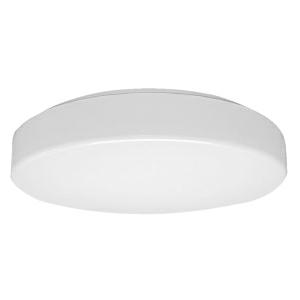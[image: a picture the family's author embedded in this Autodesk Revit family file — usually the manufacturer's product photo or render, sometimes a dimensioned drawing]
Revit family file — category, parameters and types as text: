
# Revit family: oblo_fit_-_oba_1000_840_00813345_71a7
name_source: partatom
category: Lighting Fixtures
units: mm (PartAtom-declared; Revit-internal decimal feet)

## family parameters
Cut with Voids When Loaded = No
Host = Face
Light Source = No
Part Type = Normal
Room Calculation Point = No
Round Connector Dimension = Use Diameter
Shared = No

## types (1)
- OBLO.fit - OBA 1000/840 (1 x LED, 1500 lm, 4000K)
    Apparent Load = 11 VA
    Approval mark = CE
    CIE Flux Codes = 41 72 91 84 100
    Color Rendering = 80-89
    Color Temperature = 4000K
    Control Gear = Electronic ballast
    Default Elevation = 1800 mm
    Description = OBA 1000/840|Surface-mounted luminaire.|light source:   Cold white   |work equipment: Power supply unit|luminous flux: 1500 lm|light distribution: Direct|class of protection: I|technology: Switchable|mains lead: Direct power supply|glare control: without|
    Frequency = 50 Hz, 60 Hz
    Height = 85 mm
    Lamp = 1 x LED
    Lamp Light Flux = 1500 lm
    Lamp count = 1
    Length = 300 mm
    Luminous efficacy = 136 lm/W
    Manufacturer = Waldmann
    ModVariant = No
    Model = 00813345
    Mounting Place = Ceiling
    Mounting Type = Surface mounted
    Number of Poles = 1
    OnlyDefault = Yes
    Power Factor = 1
    Product Name = OBLO.fit - OBA 1000/840
    Product group = Ceiling mounted luminaire
    ProductGroupID = 3
    Protection Class = Protection class I
    Protection Degree = IP 40
    RLX_Detail_Level = 1
    RLX_Emergency_Light_Flux = 0 lm
    RLX_Emergency_Type = 0
    RLX_Emergency_Type_DB = No
    RlxData = <blob elided: 22125 chars, md5=38a86d2c>
    Socket = socket
    Standby Power = 0 W
    System Light Flux = 1500 lm
    System Power = 11 W
    Type Comments = Product without accessories
    Type Image = oblo_led.jpg
    URL = http://relux.com
    VarID = ---
    Voltage = 230 V
    Voltage Range = 220-240 V
    Weight = 0.00 kg
    Width = 0 mm  [stored 0 ft]

note: [stored X ft] marks values corroborated as IEEE doubles in the binary element streams (Revit-internal decimal feet)

## geometry (parser evidence)
native form markers: Blend x4, Sweep x12
no freeform markers — native parametric forms only
